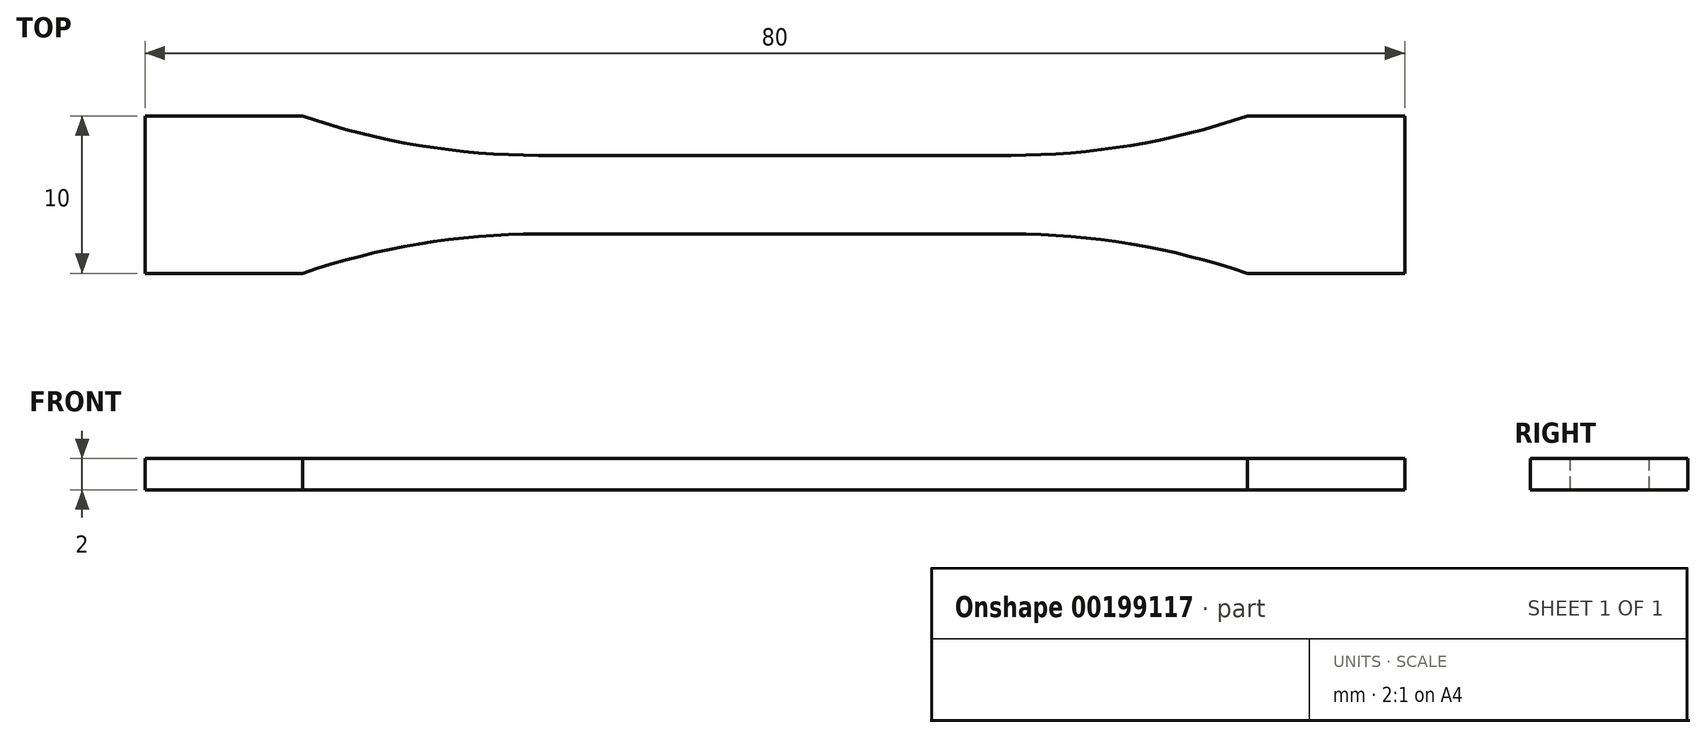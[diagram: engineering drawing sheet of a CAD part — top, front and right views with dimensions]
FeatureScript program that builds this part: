
annotation { "Feature Type Name" : "Feature", "Feature Type Description" : "" }
export const myFeature = defineFeature(function(context is Context, id is Id, definition is map)
    precondition{}
    {
        {
            var Q0;
            Q0=qCreatedBy(makeId("Top.planeOp"),FACE);
            var sketch = newSketch(context, id + "F0", { "sketchPlane" : qUnion([Q0])});
            skLineSegment(sketch, "E0", {"start": v(-30, 5) * mm, "end": v(-40, 5) * mm});
            skLineSegment(sketch, "E1", {"start": v(-40, 5) * mm, "end": v(-40, -5) * mm});
            skLineSegment(sketch, "E2", {"start": v(-40, -5) * mm, "end": v(-30, -5) * mm});
            skLineSegment(sketch, "E3", {"start": v(-15, -2.5) * mm, "end": v(0, -2.5) * mm});
            skLineSegment(sketch, "E4", {"start": v(0, -2.5) * mm, "end": v(0, 2.5) * mm, "construction": true});
            skLineSegment(sketch, "E5", {"start": v(0, 2.5) * mm, "end": v(-15, 2.5) * mm});
            skLineSegment(sketch, "E6", {"start": v(-40, 0) * mm, "end": v(0, 0) * mm, "construction": true});
            skArc(sketch, "E7", {"start": v(-30, 5) * mm, "mid": v(-22.6, 3.13) * mm, "end": v(-15, 2.5) * mm});
            skArc(sketch, "E8", {"start": v(-15, -2.5) * mm, "mid": v(-22.6, -3.13) * mm, "end": v(-30, -5) * mm});
            skLineSegment(sketch, "E9.MirrorCS", {"start": v(0, 2.5) * mm, "end": v(15, 2.5) * mm});
            skArc(sketch, "E10.MirrorCS", {"start": v(30, 5) * mm, "mid": v(22.6, 3.13) * mm, "end": v(15, 2.5) * mm});
            skLineSegment(sketch, "E11.MirrorCS", {"start": v(30, 5) * mm, "end": v(40, 5) * mm});
            skLineSegment(sketch, "E12.MirrorCS", {"start": v(40, 5) * mm, "end": v(40, -5) * mm});
            skArc(sketch, "E13.MirrorCS", {"start": v(15, -2.5) * mm, "mid": v(22.6, -3.13) * mm, "end": v(30, -5) * mm});
            skLineSegment(sketch, "E14.MirrorCS", {"start": v(15, -2.5) * mm, "end": v(0, -2.5) * mm});
            skLineSegment(sketch, "E15.MirrorCS", {"start": v(40, -5) * mm, "end": v(30, -5) * mm});
            skSolve(sketch);
        }
        {
            var Q0;
            Q0=makeQuery(id+"F0.imprint","IMPRINT",FACE,{"disambiguationData":[TD([[makeQuery(id+"F0.imprint","IMPRINT",EDGE,{"derivedFrom":sQuery(id+"F0.wireOp",EDGE,"E0")}),1.0]])]});
            extrude(context, id + "F1", {"entities" : qUnion([Q0]), "depth" : 2 * mm, "offsetDistance" : 25 * mm});
        }
    });
